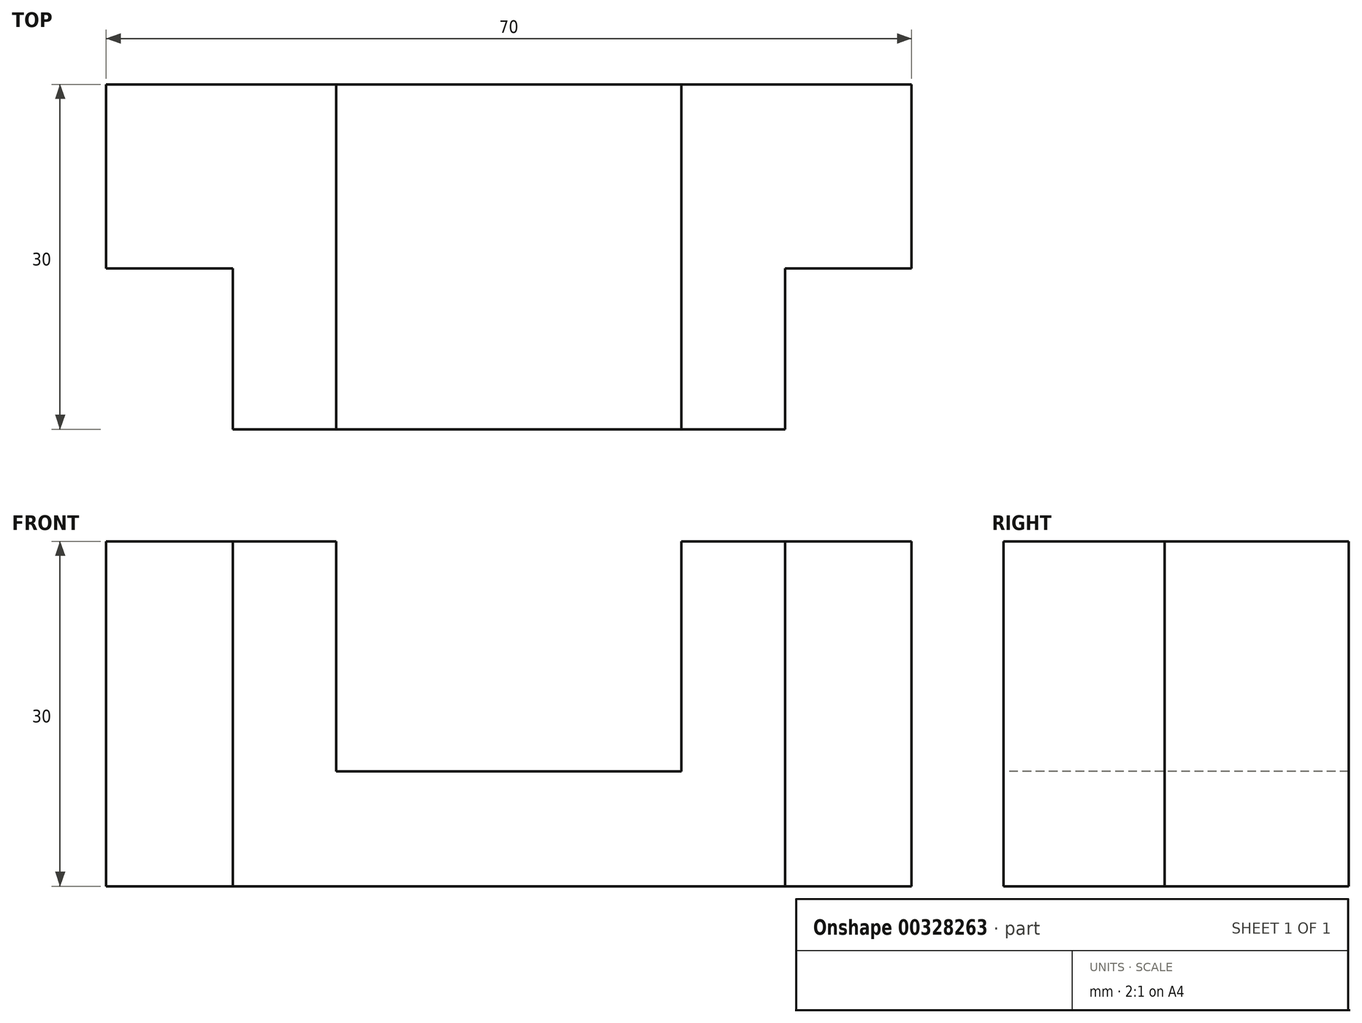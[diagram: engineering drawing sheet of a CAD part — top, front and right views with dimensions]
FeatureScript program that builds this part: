
annotation { "Feature Type Name" : "Feature", "Feature Type Description" : "" }
export const myFeature = defineFeature(function(context is Context, id is Id, definition is map)
    precondition{}
    {
        {
            var Q0;
            Q0=qCreatedBy(makeId("Top.planeOp"),FACE);
            var sketch = newSketch(context, id + "F0", { "sketchPlane" : qUnion([Q0])});
            skLineSegment(sketch, "E0", {"start": v(-24, -30) * mm, "end": v(24, -30) * mm});
            skLineSegment(sketch, "E1", {"start": v(24, -30) * mm, "end": v(24, -16) * mm});
            skLineSegment(sketch, "E2", {"start": v(24, -16) * mm, "end": v(35, -16) * mm});
            skLineSegment(sketch, "E3", {"start": v(35, -16) * mm, "end": v(35, 0) * mm});
            skLineSegment(sketch, "E4", {"start": v(35, 0) * mm, "end": v(-35, 0) * mm});
            skLineSegment(sketch, "E5", {"start": v(-35, 0) * mm, "end": v(-35, -16) * mm});
            skLineSegment(sketch, "E6", {"start": v(-35, -16) * mm, "end": v(-24, -16) * mm});
            skLineSegment(sketch, "E7", {"start": v(-24, -16) * mm, "end": v(-24, -30) * mm});
            skSolve(sketch);
        }
        {
            var Q0;
            Q0=makeQuery(id+"F0.imprint","IMPRINT",FACE,{"disambiguationData":[TD([[makeQuery(id+"F0.imprint","IMPRINT",EDGE,{"derivedFrom":sQuery(id+"F0.wireOp",EDGE,"E0")}),1.0]])]});
            extrude(context, id + "F1", {"entities" : qUnion([Q0]), "depth" : 30 * mm});
        }
        {
            var Q0;
            Q0=makeQuery(id+"F1.opExtrude","SWEPT_FACE",FACE,{"disambiguationData":[OSD([sQuery(id+"F0.wireOp",EDGE,"E0")])]});
            var sketch = newSketch(context, id + "F2", { "sketchPlane" : qUnion([Q0])});
            skLineSegment(sketch, "E8", {"start": v(-15, 33) * mm, "end": v(-15, 10) * mm});
            skLineSegment(sketch, "E9", {"start": v(-15, 10) * mm, "end": v(15, 10) * mm});
            skLineSegment(sketch, "E10", {"start": v(15, 10) * mm, "end": v(15, 33) * mm});
            skLineSegment(sketch, "E11", {"start": v(15, 33) * mm, "end": v(-15, 33) * mm});
            skSolve(sketch);
        }
        {
            var Q0;
            {var subQ0=sQuery(id+"F2.wireOp",EDGE,"E9");Q0=makeQuery(id+"F2.imprint","IMPRINT",FACE,{"disambiguationData":[TD([[makeQuery(id+"F2.imprint","IMPRINT",EDGE,{"derivedFrom":subQ0}),1.0]])]});}
            extrude(context, id + "F3", {"entities" : qUnion([Q0]), "operationType" : NewBodyOperationType.REMOVE, "oppositeDirection" : true, "depth" : 40 * mm});
        }
    });
